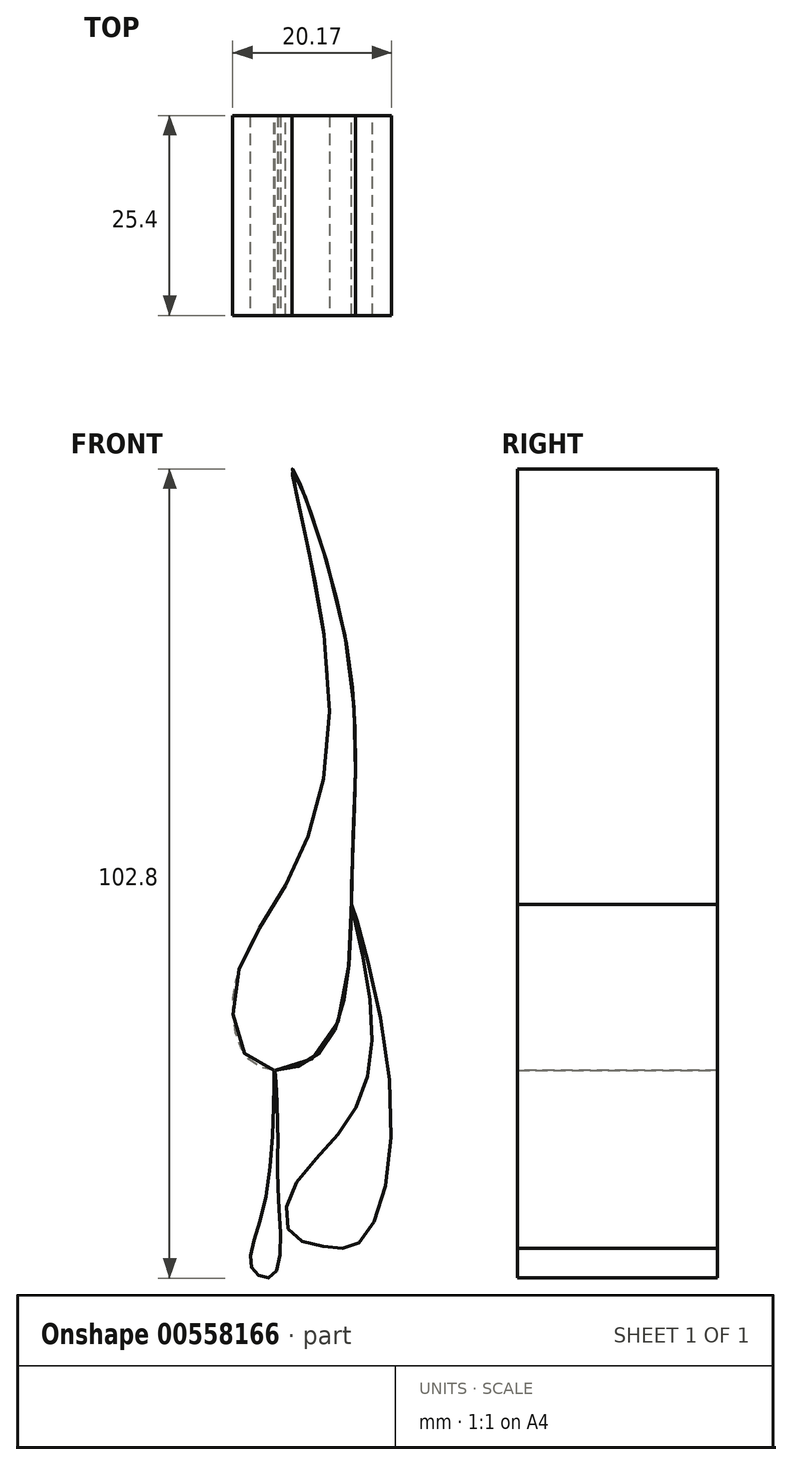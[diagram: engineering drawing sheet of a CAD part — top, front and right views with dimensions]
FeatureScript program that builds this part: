
annotation { "Feature Type Name" : "Feature", "Feature Type Description" : "" }
export const myFeature = defineFeature(function(context is Context, id is Id, definition is map)
    precondition{}
    {
        {
            var Q0;
            Q0=qCreatedBy(makeId("Front.planeOp"),FACE);
            var sketch = newSketch(context, id + "F0", { "sketchPlane" : qUnion([Q0])});
            skFitSpline(sketch, "E0", {"points": [v(0, 26.2) * mm, v(6.64, 5.46) * mm, v(7.6, -24.96) * mm, v(4.01, -47.37) * mm, v(-4.7, -49.44) * mm, v(-7.2, -39.07) * mm, v(0, -25.1) * mm, v(4.43, 1.87) * mm, v(0, 26.2) * mm]});
            skSolve(sketch);
        }
        {
            var Q0;
            Q0 = qSketchRegion(id + "F0", true);
            extrude(context, id + "F1", {"entities" : qUnion([Q0]), "endBound" : BoundingType.SYMMETRIC, "depth" : 25.4 * mm, "offsetDistance" : 25.4 * mm});
        }
        {
            var Q0;
            Q0=qCreatedBy(makeId("Front.planeOp"),FACE);
            var sketch = newSketch(context, id + "F2", { "sketchPlane" : qUnion([Q0])});
            skFitSpline(sketch, "E1", {"points": [v(7.55, -29.1) * mm, v(12.56, -53.9) * mm, v(8.42, -72.2) * mm, v(4.72, -72.63) * mm, v(0, -71.1) * mm, v(0, -65.44) * mm, v(7.33, -56.3) * mm, v(9.94, -41.5) * mm, v(7.55, -29.1) * mm]});
            skFitSpline(sketch, "E2", {"points": [v(-2.24, -50) * mm, v(-1.8, -57.6) * mm, v(-1.8, -65) * mm, v(-2.46, -76.33) * mm, v(-5.07, -75.46) * mm, v(-3.33, -66.31) * mm, v(-2.24, -50) * mm]});
            skSolve(sketch);
        }
        {
            var Q0;
            Q0=makeQuery(id+"F2.imprint","IMPRINT",FACE,{"disambiguationData":[TD([[makeQuery(id+"F2.imprint","IMPRINT",EDGE,{"derivedFrom":sQuery(id+"F2.wireOp",EDGE,"E1")}),-1.0]])]});
            var Q1;
            Q1 = qSketchRegion(id + "F2", true);
            extrude(context, id + "F3", {"entities" : qUnion([Q0, Q1]), "operationType" : NewBodyOperationType.ADD, "endBound" : BoundingType.SYMMETRIC, "depth" : 25.4 * mm, "offsetDistance" : 25.4 * mm});
        }
    });
